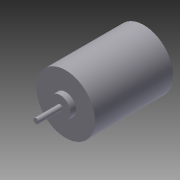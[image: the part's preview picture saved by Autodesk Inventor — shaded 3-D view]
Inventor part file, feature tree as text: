
AUTODESK INVENTOR PART (.ipt)
format: ipt  version: 2012 (Build 160160000, 160)  size: 86,528 bytes
history: native  units: mm
features: extrude x3, sketch x1
ambient origin geometry x8: Origin, YZ Plane, XZ Plane, XY Plane, X Axis, Y Axis, Z Axis, Center Point
bodies: Solid1 (feature_tree)
feature tree (4):
  sketch  "Sketch1"  dims[d0=17.1mm d1=6.15mm d2=1.5mm d3=22.8mm d4=0.0mm d5=1.6mm d6=0.0mm d7=8.6mm d8=0.0mm]
  extrude  "Extrusion1"  Depth=6.15mm
  extrude  "Extrusion2"  Depth=1.5mm
  extrude  "Extrusion3"  Depth=22.8mm TaperAngle=0.0deg
